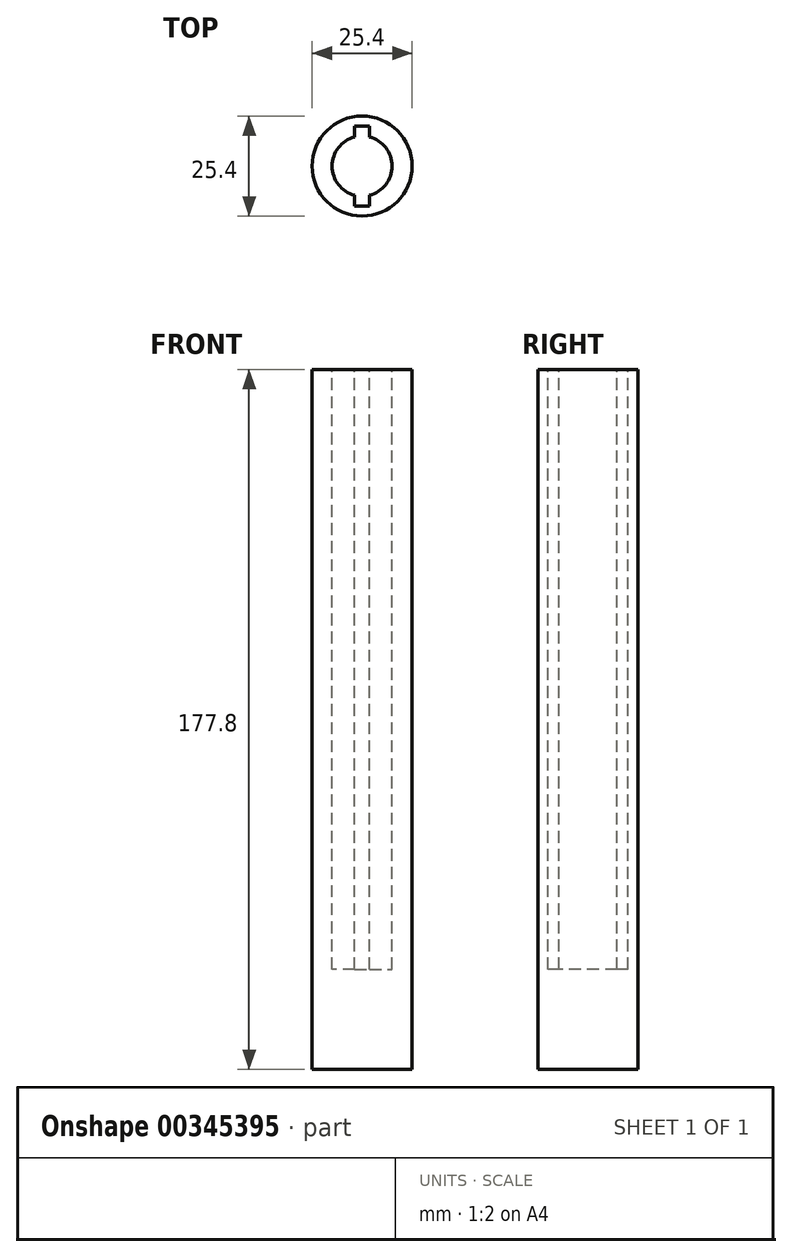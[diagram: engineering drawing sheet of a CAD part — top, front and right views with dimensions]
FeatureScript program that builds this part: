
annotation { "Feature Type Name" : "Feature", "Feature Type Description" : "" }
export const myFeature = defineFeature(function(context is Context, id is Id, definition is map)
    precondition{}
    {
        {
            var Q0;
            Q0=qCreatedBy(makeId("Top.planeOp"),FACE);
            var sketch = newSketch(context, id + "F0", { "sketchPlane" : qUnion([Q0])});
            skCircle(sketch, "E0", {"center": v(0, 0) * mm, "radius": 12.7 * mm});
            skSolve(sketch);
        }
        {
            var Q0;
            Q0=makeQuery(id+"F0.imprint","IMPRINT",FACE,{"disambiguationData":[TD([[makeQuery(id+"F0.imprint","IMPRINT",EDGE,{"derivedFrom":sQuery(id+"F0.wireOp",EDGE,"E0")}),1.0]])]});
            extrude(context, id + "F1", {"entities" : qUnion([Q0]), "depth" : 177.8 * mm});
        }
        {
            var Q0;
            Q0=makeQuery(id+"F1.opExtrude","CAP_FACE",FACE,{"disambiguationData":[OSD([sQuery(id+"F0.wireOp",EDGE,"E0")])],"isStart":false});
            var sketch = newSketch(context, id + "F2", { "sketchPlane" : qUnion([Q0])});
            skCircle(sketch, "E1", {"center": v(0, 0) * mm, "radius": 7.62 * mm});
            skLineSegment(sketch, "E2.bottom", {"start": v(-1.9, 10.16) * mm, "end": v(1.9, 10.16) * mm});
            skLineSegment(sketch, "E2.top", {"start": v(-1.9, -10.16) * mm, "end": v(1.9, -10.16) * mm});
            skLineSegment(sketch, "E2.left", {"start": v(-1.9, 10.16) * mm, "end": v(-1.9, -10.16) * mm});
            skLineSegment(sketch, "E2.right", {"start": v(1.9, 10.16) * mm, "end": v(1.9, -10.16) * mm});
            skSolve(sketch);
        }
        {
            var Q0;
            {var subQ0=sQuery(id+"F2.wireOp",EDGE,"E2.left");var subQ1=sQuery(id+"F2.wireOp",EDGE,"E1");var subQ2=makeQuery(id+"F2.imprint","INTERSECT",VERTEX,{"disambiguationData":[OD(0.0)],"derivedFrom":[subQ1,subQ0]});Q0=makeQuery(id+"F2.imprint","IMPRINT",FACE,{"disambiguationData":[TD([[makeQuery(id+"F2.imprint","IMPRINT",EDGE,{"disambiguationData":[TD([[subQ2,-1.0]])],"derivedFrom":subQ1}),1.0]])]});}
            var Q1;
            {var subQ5=sQuery(id+"F2.wireOp",EDGE,"E2.bottom");Q1=makeQuery(id+"F2.imprint","IMPRINT",FACE,{"disambiguationData":[TD([[makeQuery(id+"F2.imprint","IMPRINT",EDGE,{"derivedFrom":subQ5}),-1.0]])]});}
            var Q2;
            {var subQ0=sQuery(id+"F2.wireOp",EDGE,"E2.left");var subQ1=sQuery(id+"F2.wireOp",EDGE,"E1");var subQ2=makeQuery(id+"F2.imprint","INTERSECT",VERTEX,{"disambiguationData":[OD(0.0)],"derivedFrom":[subQ1,subQ0]});Q2=makeQuery(id+"F2.imprint","IMPRINT",FACE,{"disambiguationData":[TD([[makeQuery(id+"F2.imprint","IMPRINT",EDGE,{"disambiguationData":[TD([[subQ2,1.0]])],"derivedFrom":subQ1}),1.0]])]});}
            var Q3;
            {var subQ0=sQuery(id+"F2.wireOp",EDGE,"E2.right");var subQ1=sQuery(id+"F2.wireOp",EDGE,"E1");var subQ2=makeQuery(id+"F2.imprint","INTERSECT",VERTEX,{"disambiguationData":[OD(0.0)],"derivedFrom":[subQ1,subQ0]});Q3=makeQuery(id+"F2.imprint","IMPRINT",FACE,{"disambiguationData":[TD([[makeQuery(id+"F2.imprint","IMPRINT",EDGE,{"disambiguationData":[TD([[subQ2,1.0]])],"derivedFrom":subQ1}),1.0]])]});}
            var Q4;
            {var subQ5=sQuery(id+"F2.wireOp",EDGE,"E2.top");Q4=makeQuery(id+"F2.imprint","IMPRINT",FACE,{"disambiguationData":[TD([[makeQuery(id+"F2.imprint","IMPRINT",EDGE,{"derivedFrom":subQ5}),1.0]])]});}
            extrude(context, id + "F3", {"entities" : qUnion([Q0, Q1, Q2, Q3, Q4]), "operationType" : NewBodyOperationType.REMOVE, "oppositeDirection" : true, "depth" : 152.4 * mm});
        }
    });
